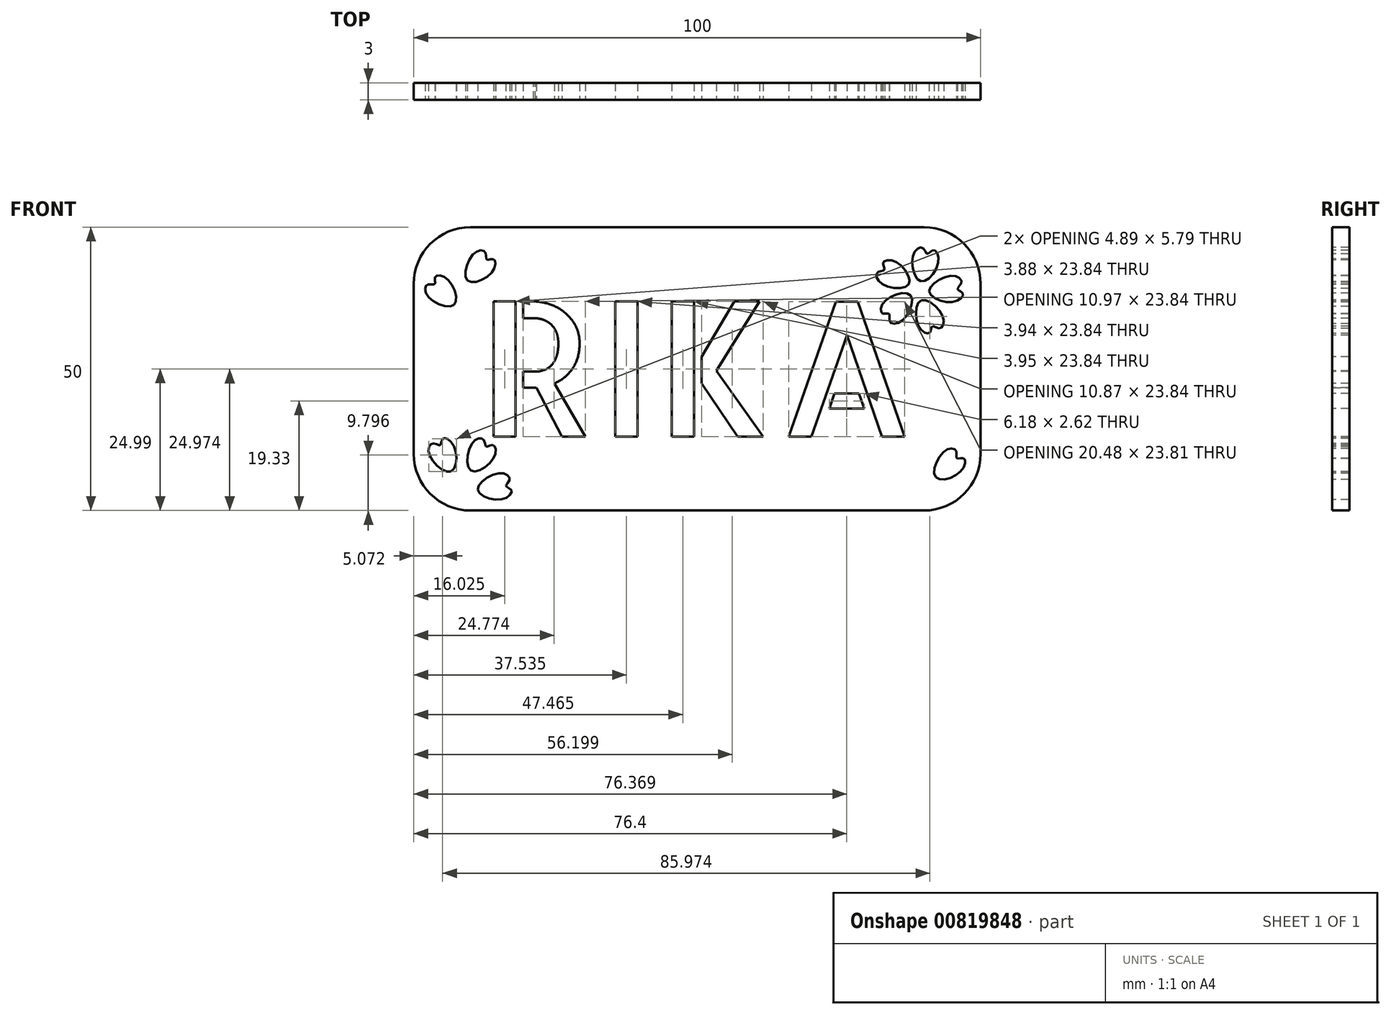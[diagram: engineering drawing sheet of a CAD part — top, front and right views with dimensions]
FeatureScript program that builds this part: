
annotation { "Feature Type Name" : "Feature", "Feature Type Description" : "" }
export const myFeature = defineFeature(function(context is Context, id is Id, definition is map)
    precondition{}
    {
        {
            var Q0;
            Q0=qCreatedBy(makeId("Front.planeOp"),FACE);
            var sketch = newSketch(context, id + "F0", { "sketchPlane" : qUnion([Q0])});
            skLineSegment(sketch, "E0.bottom", {"start": v(-50, 50) * mm, "end": v(50, 50) * mm});
            skLineSegment(sketch, "E0.top", {"start": v(-50, 0) * mm, "end": v(50, 0) * mm});
            skLineSegment(sketch, "E0.left", {"start": v(-50, 50) * mm, "end": v(-50, 0) * mm});
            skLineSegment(sketch, "E0.right", {"start": v(50, 50) * mm, "end": v(50, 0) * mm});
            skPoint(sketch, "E1", {"position": v(0, 0) * mm});
            skSolve(sketch);
        }
        {
            var Q0;
            Q0 = qSketchRegion(id + "F0", true);
            extrude(context, id + "F1", {"entities" : qUnion([Q0]), "endBound" : BoundingType.SYMMETRIC, "depth" : 3 * mm, "offsetDistance" : 25 * mm});
        }
        {
            var Q0;
            Q0=makeQuery(id+"F1.opExtrude","SWEPT_EDGE",EDGE,{"disambiguationData":[OSD([sQuery(id+"F0.wireOp",EDGE,"E0.bottom"),sQuery(id+"F0.wireOp",EDGE,"E0.left")])]});
            var Q1;
            Q1=makeQuery(id+"F1.opExtrude","SWEPT_EDGE",EDGE,{"disambiguationData":[OSD([sQuery(id+"F0.wireOp",EDGE,"E0.bottom"),sQuery(id+"F0.wireOp",EDGE,"E0.right")])]});
            var Q2;
            Q2=makeQuery(id+"F1.opExtrude","SWEPT_EDGE",EDGE,{"disambiguationData":[OSD([sQuery(id+"F0.wireOp",EDGE,"E0.top"),sQuery(id+"F0.wireOp",EDGE,"E0.right")])]});
            var Q3;
            Q3=makeQuery(id+"F1.opExtrude","SWEPT_EDGE",EDGE,{"disambiguationData":[OSD([sQuery(id+"F0.wireOp",EDGE,"E0.top"),sQuery(id+"F0.wireOp",EDGE,"E0.left")])]});
            fillet(context, id + "F2", {"entities" : qUnion([Q0, Q1, Q2, Q3]), "radius" : 10 * mm, "tangentPropagation" : true, "allowEdgeOverflow" : false});
        }
        {
            var Q0;
            Q0=makeQuery(id+"F1.opExtrude","CAP_FACE",FACE,{"disambiguationData":[OSD([sQuery(id+"F0.wireOp",EDGE,"E0.bottom"),sQuery(id+"F0.wireOp",EDGE,"E0.top"),sQuery(id+"F0.wireOp",EDGE,"E0.left"),sQuery(id+"F0.wireOp",EDGE,"E0.right")])],"isStart":false});
            var sketch = newSketch(context, id + "F3", { "sketchPlane" : qUnion([Q0])});
            skText(sketch, "E2", { "text": "RIKA", "fontName": "AllertaStencil-Regular.ttf"});
            skPoint(sketch, "E3", {"position": v(-38.83, 25) * mm});
            const initialGuessF3  = {"E2": [-0.03883, 0.01307, 1, 0, 0.02385]};
            skSetInitialGuess(sketch, initialGuessF3);
            skSolve(sketch);
        }
        {
            var Q0;
            Q0 = qSketchRegion(id + "F3", true);
            extrude(context, id + "F4", {"entities" : qUnion([Q0]), "operationType" : NewBodyOperationType.REMOVE, "oppositeDirection" : true, "depth" : 3 * mm, "offsetDistance" : 25 * mm});
        }
        {
            var Q0;
            Q0=makeQuery(id+"F1.opExtrude","CAP_FACE",FACE,{"disambiguationData":[OSD([sQuery(id+"F0.wireOp",EDGE,"E0.bottom"),sQuery(id+"F0.wireOp",EDGE,"E0.top"),sQuery(id+"F0.wireOp",EDGE,"E0.left"),sQuery(id+"F0.wireOp",EDGE,"E0.right")])],"isStart":false});
            var sketch = newSketch(context, id + "F5", { "sketchPlane" : qUnion([Q0])});
            skFitSpline(sketch, "E4", {"points": [v(39.43, 40.46) * mm, v(38.14, 45.22) * mm, v(39.8, 46.32) * mm, v(40.62, 45.31) * mm, v(41.63, 45.96) * mm, v(42.54, 43.94) * mm, v(39.43, 40.46) * mm]});
            skFitSpline(sketch, "E5", {"points": [v(37.31, 39.9) * mm, v(32.39, 40.14) * mm, v(31.85, 42.05) * mm, v(33.06, 42.52) * mm, v(32.77, 43.68) * mm, v(34.96, 43.93) * mm, v(37.31, 39.9) * mm]});
            skFitSpline(sketch, "E6", {"points": [v(37.68, 37.95) * mm, v(35.91, 33.34) * mm, v(33.93, 33.42) * mm, v(33.86, 34.72) * mm, v(32.67, 34.8) * mm, v(33.11, 36.96) * mm, v(37.68, 37.95) * mm]});
            skFitSpline(sketch, "E7", {"points": [v(39.58, 37.13) * mm, v(43.42, 34.03) * mm, v(42.73, 32.17) * mm, v(41.47, 32.5) * mm, v(41.03, 31.39) * mm, v(39.1, 32.48) * mm, v(39.58, 37.13) * mm]});
            skFitSpline(sketch, "E8", {"points": [v(40.94, 38.72) * mm, v(45.08, 41.42) * mm, v(46.63, 40.19) * mm, v(45.93, 39.1) * mm, v(46.85, 38.33) * mm, v(45.22, 36.84) * mm, v(40.94, 38.72) * mm]});
            skFitSpline(sketch, "E9", {"points": [v(-39.93, 7.08) * mm, v(-39.6, 12) * mm, v(-37.68, 12.5) * mm, v(-37.23, 11.28) * mm, v(-36.06, 11.56) * mm, v(-35.86, 9.36) * mm, v(-39.93, 7.08) * mm]});
            skFitSpline(sketch, "E10", {"points": [v(-43.46, 6.9) * mm, v(-47.3, 10) * mm, v(-46.61, 11.86) * mm, v(-45.35, 11.53) * mm, v(-44.91, 12.64) * mm, v(-43, 11.55) * mm, v(-43.46, 6.9) * mm]});
            skFitSpline(sketch, "E11", {"points": [v(-40.53, 40.61) * mm, v(-39.34, 45.4) * mm, v(-37.36, 45.57) * mm, v(-37.13, 44.28) * mm, v(-35.94, 44.36) * mm, v(-36.11, 42.15) * mm, v(-40.53, 40.61) * mm]});
            skFitSpline(sketch, "E12", {"points": [v(-42.92, 36.3) * mm, v(-47.59, 37.9) * mm, v(-47.58, 39.88) * mm, v(-46.28, 40) * mm, v(-46.25, 41.2) * mm, v(-44.07, 40.83) * mm, v(-42.92, 36.3) * mm]});
            skFitSpline(sketch, "E13", {"points": [v(42.1, 5.88) * mm, v(43.7, 10.55) * mm, v(45.68, 10.54) * mm, v(45.8, 9.24) * mm, v(47, 9.2) * mm, v(46.62, 7.03) * mm, v(42.1, 5.88) * mm]});
            skFitSpline(sketch, "E14", {"points": [v(-38.7, 3.7) * mm, v(-34.7, 6.6) * mm, v(-33.09, 5.46) * mm, v(-33.73, 4.33) * mm, v(-32.77, 3.61) * mm, v(-34.32, 2.04) * mm, v(-38.7, 3.7) * mm]});
            skSolve(sketch);
        }
        {
            var Q0;
            Q0 = qSketchRegion(id + "F5", true);
            extrude(context, id + "F6", {"entities" : qUnion([Q0]), "operationType" : NewBodyOperationType.REMOVE, "oppositeDirection" : true, "depth" : 3 * mm, "offsetDistance" : 25 * mm});
        }
    });
